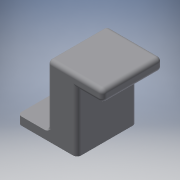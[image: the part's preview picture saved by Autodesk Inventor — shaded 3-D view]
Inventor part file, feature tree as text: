
AUTODESK INVENTOR PART (.ipt)
format: ipt  version: 2018 (Build 220112000, 112)  size: 171,008 bytes
history: native  units: mm
features: extrude x4, sketch x4, fillet x3, projected_geometry x2
ambient origin geometry x8: Origin, YZ Plane, XZ Plane, XY Plane, X Axis, Y Axis, Z Axis, Center Point
bodies: Solid1 (feature_tree)
feature tree (13):
  extrude  "Extrusion1"  Depth=15.0mm
  extrude  "Extrusion2"  Depth=7.5mm
  extrude  "Extrusion3"  Depth=14.0mm
  extrude  "Extrusion4"  Depth=1.0mm
  fillet  "Fillet1"  Radius=2.5mm
  fillet  "Fillet2"  Radius=3.0mm
  fillet  "Fillet3"  Radius=1.0mm
  sketch  "Sketch1"  dims[d0=15.0mm d1=15.0mm]
  sketch  "Sketch2"  dims[d2=2.0mm d3=0.0mm d4=7.5mm]
  sketch  "Sketch3"  dims[d5=10.8mm d6=0.0mm d7=14.0mm]
  sketch  "Sketch4"  dims[d8=3.0mm d9=0.0mm d10=4.0mm d11=2.5mm d12=3.0mm d13=0.0mm d14=1.0mm d15=1.0mm d16=1.0mm]
  projected_geometry  "Projected Loop1"
  projected_geometry  "Projected Loop2"
